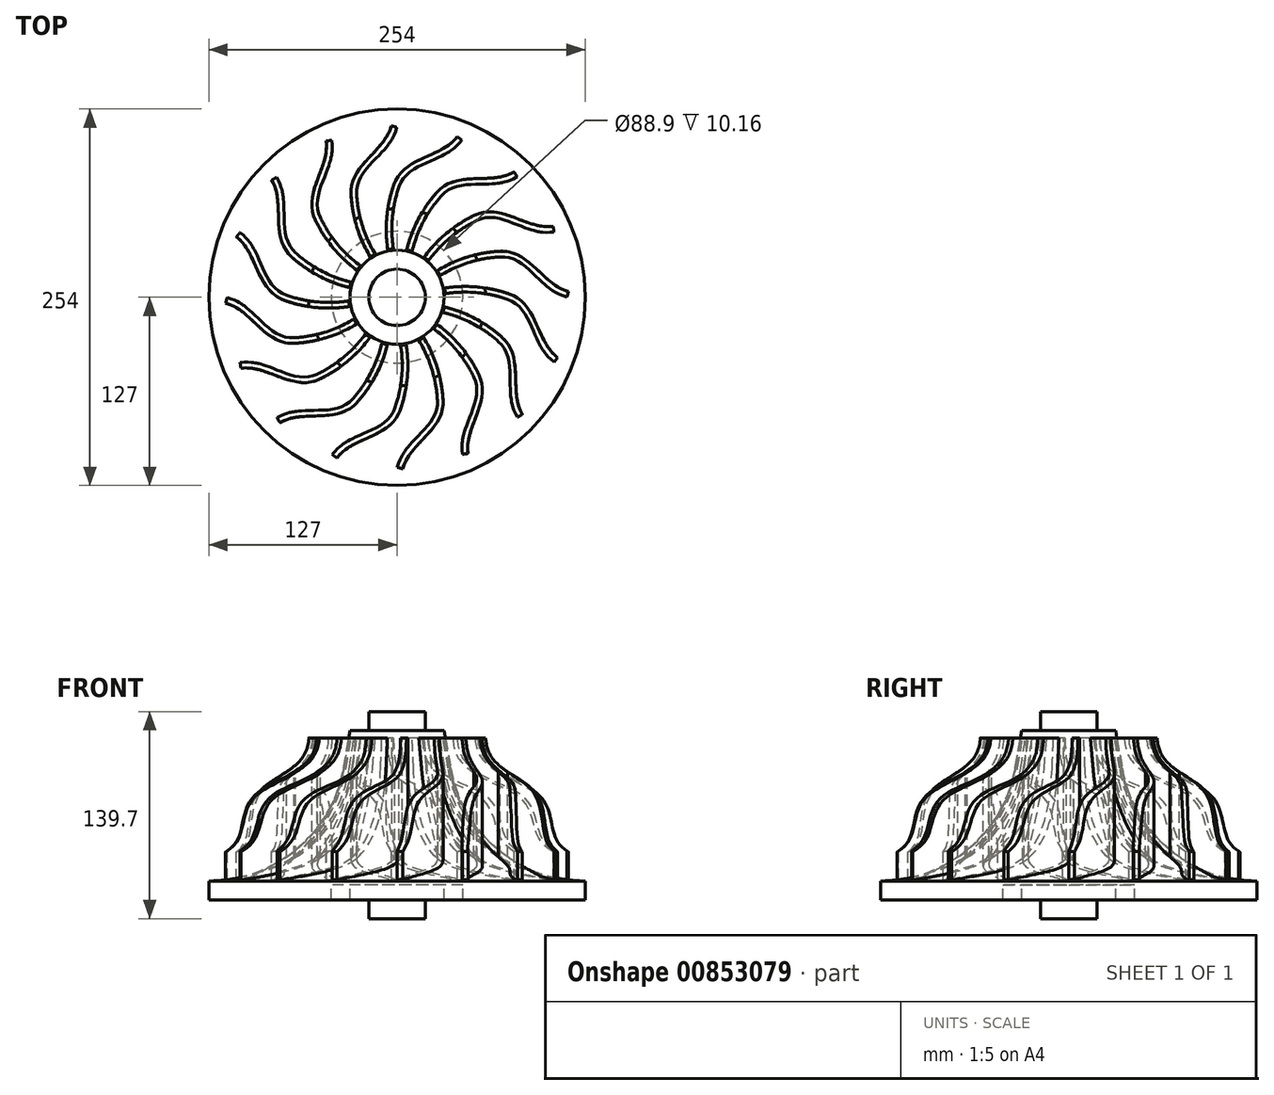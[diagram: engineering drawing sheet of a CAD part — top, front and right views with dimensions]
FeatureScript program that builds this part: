
annotation { "Feature Type Name" : "Feature", "Feature Type Description" : "" }
export const myFeature = defineFeature(function(context is Context, id is Id, definition is map)
    precondition{}
    {
        {
            var Q0;
            Q0=qCreatedBy(makeId("Front.planeOp"),FACE);
            var sketch = newSketch(context, id + "F0", { "sketchPlane" : qUnion([Q0])});
            skLineSegment(sketch, "E0", {"start": v(19.05, 5.13) * mm, "end": v(31.75, 5.13) * mm});
            skLineSegment(sketch, "E1", {"start": v(19.05, -109.17) * mm, "end": v(31.75, -109.17) * mm});
            skLineSegment(sketch, "E2", {"start": v(0, 17.83) * mm, "end": v(0, -121.87) * mm});
            skLineSegment(sketch, "E3", {"start": v(31.75, 5.13) * mm, "end": v(36.24, -20.3) * mm});
            skLineSegment(sketch, "E4", {"start": v(127, -109.17) * mm, "end": v(127, -96.47) * mm});
            skArc(sketch, "E5", {"start": v(36.24, -20.3) * mm, "mid": v(67.76, -74.9) * mm, "end": v(127, -96.47) * mm});
            skLineSegment(sketch, "E6", {"start": v(127, -96.47) * mm, "end": v(236.69, -96.47) * mm, "construction": true});
            skLineSegment(sketch, "E7.top", {"start": v(0, 17.83) * mm, "end": v(19.05, 17.83) * mm});
            skLineSegment(sketch, "E7.right", {"start": v(19.05, 5.13) * mm, "end": v(19.05, 17.83) * mm});
            skLineSegment(sketch, "E8.top", {"start": v(19.05, -121.87) * mm, "end": v(0, -121.87) * mm});
            skLineSegment(sketch, "E9", {"start": v(19.05, -121.87) * mm, "end": v(19.05, -109.17) * mm});
            skLineSegment(sketch, "E10.bottom", {"start": v(31.75, -99) * mm, "end": v(44.45, -99) * mm});
            skLineSegment(sketch, "E10.left", {"start": v(31.75, -99) * mm, "end": v(31.75, -109.17) * mm});
            skLineSegment(sketch, "E10.right", {"start": v(44.45, -99) * mm, "end": v(44.45, -109.17) * mm});
            skLineSegment(sketch, "E11.trimOffspring", {"start": v(44.45, -109.17) * mm, "end": v(127, -109.17) * mm});
            skPoint(sketch, "E12.bottom.start.orphan", {"position": v(38.1, -109.17) * mm});
            skSolve(sketch);
        }
        {
            var Q0;
            Q0 = qSketchRegion(id + "F0", true);
            var Q1;
            Q1=sQuery(id+"F0.wireOp",EDGE,"E2");
            revolve(context, id + "F1", {"surfaceOperationType" : NewSurfaceOperationType.NEW, "entities" : qUnion([Q0]), "axis" : qUnion([Q1]), "revolveType" : RevolveType.FULL});
        }
        {
            var Q0;
            Q0=qCreatedBy(makeId("Top.planeOp"),FACE);
            var sketch = newSketch(context, id + "F2", { "sketchPlane" : qUnion([Q0])});
            skArc(sketch, "E13", {"start": v(27.1, 71) * mm, "mid": v(9.03, 40.47) * mm, "end": v(4.23, 5.32) * mm});
            skFitSpline(sketch, "E14", {"points": [v(27.1, 71) * mm, v(79.07, 84.55) * mm], "startDerivative": vector(40.65, 45.08) * mm, "endDerivative": vector(47.33, 27.48) * mm});
            skArc(sketch, "E15.0", {"start": v(29.93, 68.46) * mm, "mid": v(12.62, 39.22) * mm, "end": v(8.03, 5.56) * mm});
            skFitSpline(sketch, "E15.1", {"points": [v(29.93, 68.46) * mm, v(30.65, 69.26) * mm, v(32.13, 70.67) * mm, v(34.5, 72.32) * mm, v(37.04, 73.6) * mm, v(40.67, 74.89) * mm, v(45.68, 75.82) * mm, v(52.33, 76.22) * mm, v(59.37, 76.35) * mm, v(66.62, 76.75) * mm, v(72.71, 77.82) * mm, v(77.5, 79.45) * mm, v(79.84, 80.6) * mm, v(80.98, 81.26) * mm]});
            skLineSegment(sketch, "E16", {"start": v(4.23, 5.32) * mm, "end": v(8.03, 5.56) * mm});
            skLineSegment(sketch, "E17", {"start": v(79.07, 84.55) * mm, "end": v(80.98, 81.26) * mm});
            skSolve(sketch);
        }
        {
            var Q0;
            Q0=makeQuery(id+"F2.imprint","IMPRINT",FACE,{"disambiguationData":[TD([[makeQuery(id+"F2.imprint","IMPRINT",EDGE,{"derivedFrom":sQuery(id+"F2.wireOp",EDGE,"E13")}),1.0]])]});
            var Q1;
            Q1=makeQuery(id+"F1.opRevolve","SWEPT_FACE",FACE,{"disambiguationData":[OSD([sQuery(id+"F0.wireOp",EDGE,"E5")])]});
            extrude(context, id + "F3", {"entities" : qUnion([Q0]), "oppositeDirection" : true, "depth" : 97.8 * mm, "endBoundEntityFace" : qUnion([Q1]), "offsetDistance" : 25.4 * mm});
        }
        {
            var Q0;
            Q0=makeQuery(id+"F3.opExtrude","SWEPT_BODY",BODY,{"disambiguationData":[OSD([sQuery(id+"F2.wireOp",EDGE,"E13"),sQuery(id+"F2.wireOp",EDGE,"E14"),sQuery(id+"F2.wireOp",EDGE,"E15.0"),sQuery(id+"F2.wireOp",EDGE,"E15.1"),sQuery(id+"F2.wireOp",EDGE,"E16"),sQuery(id+"F2.wireOp",EDGE,"E17")])]});
            var Q1;
            Q1=sQuery(id+"F0.wireOp",EDGE,"E2");
            circularPattern(context, id + "F4", {"operationType" : NewBodyOperationType.ADD, "entities" : qUnion([Q0]), "axis" : qUnion([Q1]), "angle" : 360 * degree, "instanceCount" : 16, "equalSpace" : true});
        }
        {
            var Q0;
            Q0=qCreatedBy(makeId("Right.planeOp"),FACE);
            var sketch = newSketch(context, id + "F5", { "sketchPlane" : qUnion([Q0])});
            skFitSpline(sketch, "E18", {"points": [v(61.46, 20.83) * mm, v(64.45, -13.79) * mm, v(98.6, -41.01) * mm, v(108.51, -70.13) * mm, v(135.1, -84.14) * mm], "startDerivative": vector(-23.24, -151.87) * mm, "endDerivative": vector(140.32, -40.87) * mm});
            skLineSegment(sketch, "E19", {"start": v(135.1, 20.83) * mm, "end": v(61.46, 20.83) * mm});
            skLineSegment(sketch, "E20", {"start": v(135.1, 20.83) * mm, "end": v(135.1, -84.14) * mm});
            skSolve(sketch);
        }
        {
            var Q0;
            Q0=makeQuery(id+"F5.imprint","IMPRINT",FACE,{"disambiguationData":[TD([[makeQuery(id+"F5.imprint","IMPRINT",EDGE,{"derivedFrom":sQuery(id+"F5.wireOp",EDGE,"E18")}),1.0]])]});
            var Q1;
            Q1=sQuery(id+"F0.wireOp",EDGE,"E2");
            revolve(context, id + "F6", {"surfaceOperationType" : NewSurfaceOperationType.NEW, "entities" : qUnion([Q0]), "axis" : qUnion([Q1]), "revolveType" : RevolveType.FULL});
        }
        {
            var Q0;
            Q0=makeQuery(id+"F6.opRevolve","SWEPT_BODY",BODY,{"disambiguationData":[OSD([sQuery(id+"F5.wireOp",EDGE,"E18"),sQuery(id+"F5.wireOp",EDGE,"E19"),sQuery(id+"F5.wireOp",EDGE,"E20")])]});
            var Q1;
            Q1=makeQuery(id+"F1.opRevolve","SWEPT_BODY",BODY,{"disambiguationData":[OSD([sQuery(id+"F0.wireOp",EDGE,"E0"),sQuery(id+"F0.wireOp",EDGE,"E1"),sQuery(id+"F0.wireOp",EDGE,"E2"),sQuery(id+"F0.wireOp",EDGE,"E3"),sQuery(id+"F0.wireOp",EDGE,"E4"),sQuery(id+"F0.wireOp",EDGE,"E5"),sQuery(id+"F0.wireOp",EDGE,"E7.top"),sQuery(id+"F0.wireOp",EDGE,"E7.right"),sQuery(id+"F0.wireOp",EDGE,"E8.top"),sQuery(id+"F0.wireOp",EDGE,"E9"),sQuery(id+"F0.wireOp",EDGE,"E10.bottom"),sQuery(id+"F0.wireOp",EDGE,"E10.left"),sQuery(id+"F0.wireOp",EDGE,"E10.right"),sQuery(id+"F0.wireOp",EDGE,"E11.trimOffspring")])]});
            booleanBodies(context, id + "F7", {"operationType" : BooleanOperationType.SUBTRACTION, "tools" : qUnion([Q0]), "targets" : qUnion([Q1])});
        }
    });
